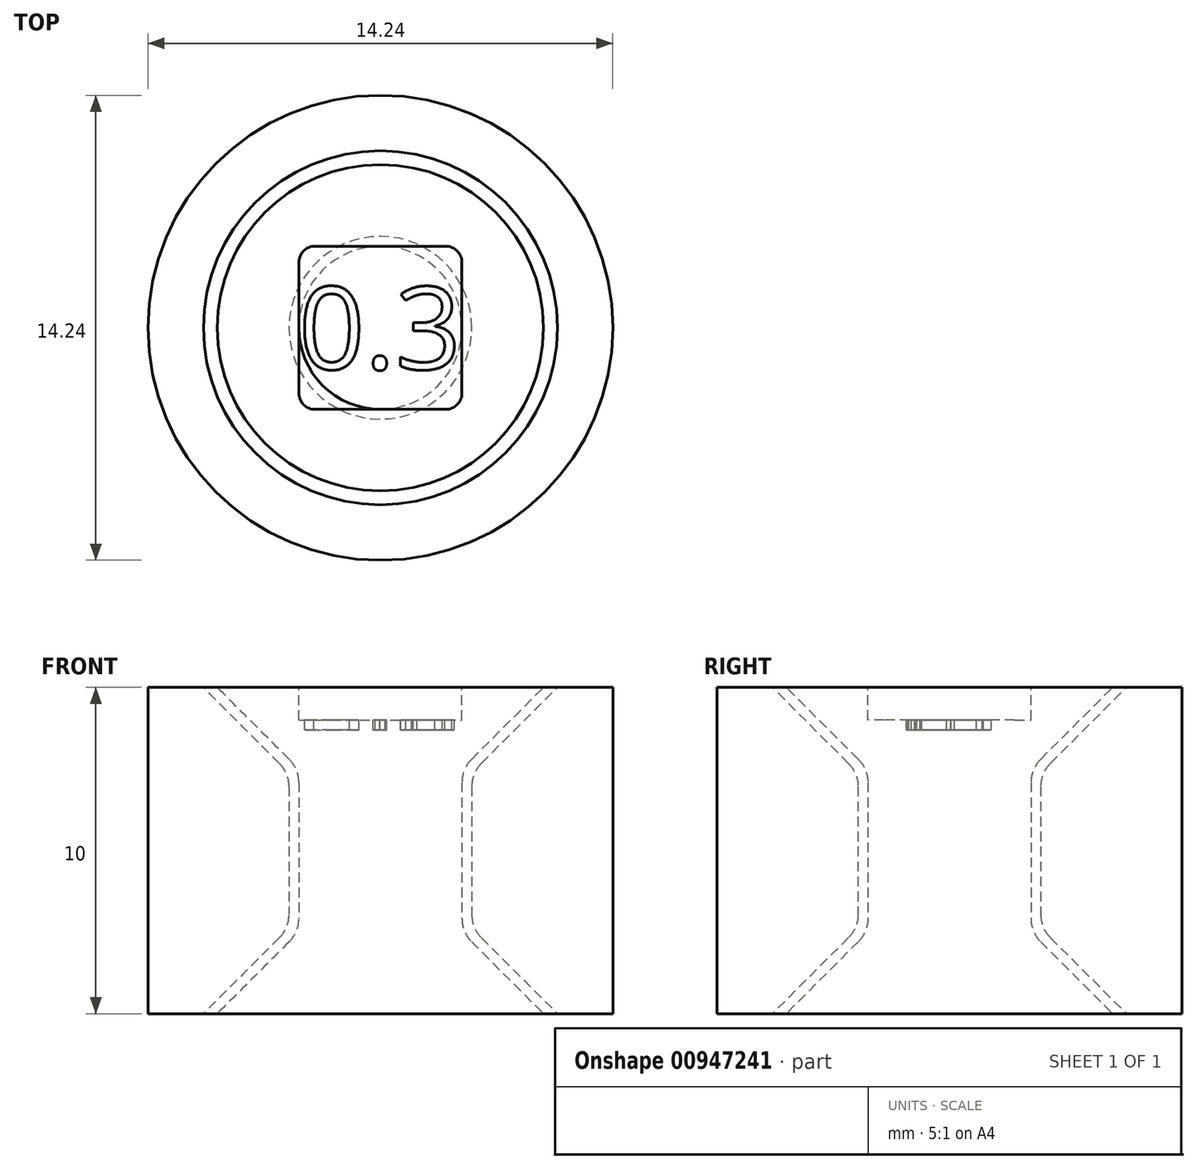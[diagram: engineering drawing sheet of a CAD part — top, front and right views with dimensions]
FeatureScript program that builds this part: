
annotation { "Feature Type Name" : "Feature", "Feature Type Description" : "" }
export const myFeature = defineFeature(function(context is Context, id is Id, definition is map)
    precondition{}
    {
        {
            var Q0;
            Q0=qCreatedBy(makeId("Front.planeOp"),FACE);
            var sketch = newSketch(context, id + "F0", { "sketchPlane" : qUnion([Q0])});
            skLineSegment(sketch, "E0", {"start": v(0, 0) * mm, "end": v(0, 10) * mm});
            skLineSegment(sketch, "E1", {"start": v(0, 10) * mm, "end": v(-5, 10) * mm});
            skLineSegment(sketch, "E2", {"start": v(-5, 10) * mm, "end": v(-2.8, 7.8) * mm});
            skLineSegment(sketch, "E3", {"start": v(-2.5, 7.09) * mm, "end": v(-2.5, 2.91) * mm});
            skLineSegment(sketch, "E4", {"start": v(-2.8, 2.2) * mm, "end": v(-5, 0) * mm});
            skLineSegment(sketch, "E5", {"start": v(-5, 0) * mm, "end": v(0, 0) * mm});
            skLineSegment(sketch, "E6", {"start": v(-7.12, 0) * mm, "end": v(-7.12, 10) * mm});
            skLineSegment(sketch, "E7", {"start": v(-7.12, 10) * mm, "end": v(-5.42, 10) * mm});
            skLineSegment(sketch, "E8", {"start": v(-5.42, 10) * mm, "end": v(-3.1, 7.67) * mm});
            skLineSegment(sketch, "E9", {"start": v(-2.8, 6.96) * mm, "end": v(-2.8, 3.04) * mm});
            skLineSegment(sketch, "E10", {"start": v(-3.1, 2.33) * mm, "end": v(-5.42, 0) * mm});
            skLineSegment(sketch, "E11", {"start": v(-5.42, 0) * mm, "end": v(-7.12, 0) * mm});
            skPoint(sketch, "E12.visualSharp", {"position": v(-2.8, 7.38) * mm});
            skArc(sketch, "E12.filletArc", {"start": v(-2.8, 6.96) * mm, "mid": v(-2.88, 7.34) * mm, "end": v(-3.1, 7.67) * mm});
            skPoint(sketch, "E13.visualSharp", {"position": v(-2.5, 7.5) * mm});
            skArc(sketch, "E13.filletArc", {"start": v(-2.5, 7.09) * mm, "mid": v(-2.58, 7.47) * mm, "end": v(-2.8, 7.8) * mm});
            skPoint(sketch, "E14.visualSharp", {"position": v(-2.8, 2.62) * mm});
            skArc(sketch, "E14.filletArc", {"start": v(-3.1, 2.33) * mm, "mid": v(-2.88, 2.66) * mm, "end": v(-2.8, 3.04) * mm});
            skPoint(sketch, "E15.visualSharp", {"position": v(-2.5, 2.5) * mm});
            skArc(sketch, "E15.filletArc", {"start": v(-2.8, 2.2) * mm, "mid": v(-2.58, 2.53) * mm, "end": v(-2.5, 2.91) * mm});
            skSolve(sketch);
        }
        {
            var Q0;
            Q0=makeQuery(id+"F0.imprint","IMPRINT",FACE,{"disambiguationData":[TD([[makeQuery(id+"F0.imprint","IMPRINT",EDGE,{"derivedFrom":sQuery(id+"F0.wireOp",EDGE,"E0")}),1.0]])]});
            var Q1;
            Q1=makeQuery(id+"F0.imprint","IMPRINT",FACE,{"disambiguationData":[TD([[makeQuery(id+"F0.imprint","IMPRINT",EDGE,{"derivedFrom":sQuery(id+"F0.wireOp",EDGE,"E6")}),-1.0]])]});
            var Q2;
            Q2=sQuery(id+"F0.wireOp",EDGE,"E0");
            revolve(context, id + "F1", {"surfaceOperationType" : NewSurfaceOperationType.NEW, "entities" : qUnion([Q0, Q1]), "axis" : qUnion([Q2]), "revolveType" : RevolveType.FULL});
        }
        {
            var Q0;
            Q0=makeQuery(id+"F1.opRevolve","SWEPT_FACE",FACE,{"disambiguationData":[OSD([sQuery(id+"F0.wireOp",EDGE,"E1")])]});
            cPlane(context, id + "F2", {"entities" : qUnion([Q0]), "cplaneType" : CPlaneType.OFFSET, "offset" : 0 * mm, "width" : 150 * mm, "height" : 150 * mm});
        }
        {
            var Q0;
            Q0=makeQuery(id+"F1.opRevolve","SWEPT_FACE",FACE,{"disambiguationData":[OSD([sQuery(id+"F0.wireOp",EDGE,"E1")])]});
            var sketch = newSketch(context, id + "F3", { "sketchPlane" : qUnion([Q0])});
            skLineSegment(sketch, "E16.bottom", {"start": v(-2, 2.5) * mm, "end": v(2, 2.5) * mm});
            skLineSegment(sketch, "E16.top", {"start": v(-2, -2.5) * mm, "end": v(2, -2.5) * mm});
            skLineSegment(sketch, "E16.left", {"start": v(-2.5, 2) * mm, "end": v(-2.5, -2) * mm});
            skLineSegment(sketch, "E16.right", {"start": v(2.5, 2) * mm, "end": v(2.5, -2) * mm});
            skPoint(sketch, "E17.visualSharp", {"position": v(-2.5, 2.5) * mm});
            skArc(sketch, "E17.filletArc", {"start": v(-2, 2.5) * mm, "mid": v(-2.35, 2.35) * mm, "end": v(-2.5, 2) * mm});
            skPoint(sketch, "E18.visualSharp", {"position": v(-2.5, -2.5) * mm});
            skArc(sketch, "E18.filletArc", {"start": v(-2.5, -2) * mm, "mid": v(-2.35, -2.35) * mm, "end": v(-2, -2.5) * mm});
            skPoint(sketch, "E19.visualSharp", {"position": v(2.5, -2.5) * mm});
            skArc(sketch, "E19.filletArc", {"start": v(2, -2.5) * mm, "mid": v(2.35, -2.35) * mm, "end": v(2.5, -2) * mm});
            skPoint(sketch, "E20.visualSharp", {"position": v(2.5, 2.5) * mm});
            skArc(sketch, "E20.filletArc", {"start": v(2.5, 2) * mm, "mid": v(2.35, 2.35) * mm, "end": v(2, 2.5) * mm});
            skPoint(sketch, "E21", {"position": v(0, 0) * mm});
            skPoint(sketch, "E22", {"position": v(-2.5, 0) * mm});
            skPoint(sketch, "E23", {"position": v(0, 2.5) * mm});
            skSolve(sketch);
        }
        {
            var Q0;
            Q0=makeQuery(id+"F3.imprint","IMPRINT",FACE,{"disambiguationData":[TD([[makeQuery(id+"F3.imprint","IMPRINT",EDGE,{"derivedFrom":sQuery(id+"F3.wireOp",EDGE,"E16.bottom")}),-1.0]])]});
            extrude(context, id + "F4", {"entities" : qUnion([Q0]), "operationType" : NewBodyOperationType.REMOVE, "oppositeDirection" : true, "depth" : 1 * mm, "offsetDistance" : 25 * mm});
        }
        {
            var Q0;
            Q0=qCreatedBy(id+"F2.planeOp",FACE);
            var sketch = newSketch(context, id + "F5", { "sketchPlane" : qUnion([Q0])});
            skText(sketch, "E24", { "text": "0.3\n", "fontName": "OpenSans-Regular.ttf"});
            skPoint(sketch, "E25", {"position": v(-2.5, 0) * mm});
            const initialGuessF5  = {"E24": [-0.0025, -0.00127, 1, 0, 0.00254]};
            skSetInitialGuess(sketch, initialGuessF5);
            skSolve(sketch);
        }
        {
            var Q0;
            Q0=qSketchRegion(id+"F5",true);
            extrude(context, id + "F6", {"entities" : qUnion([Q0]), "operationType" : NewBodyOperationType.REMOVE, "oppositeDirection" : true, "depth" : 1.3 * mm, "offsetDistance" : 25 * mm});
        }
    });
